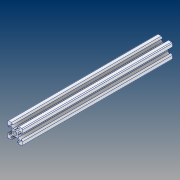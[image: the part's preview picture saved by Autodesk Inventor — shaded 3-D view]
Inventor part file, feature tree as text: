
AUTODESK INVENTOR PART (.ipt)
format: ipt  version: 2021 (Build 250183000, 183)  size: 164,352 bytes
history: native  units: mm
features: extrude x1, sketch x1
ambient origin geometry x8: Origin, YZ Plane, XZ Plane, XY Plane, X Axis, Y Axis, Z Axis, Center Point
bodies: Solid1 (feature_tree)
feature tree (2):
  extrude  "Extrusion1"  Depth=200.0mm TaperAngle=0.0deg
  sketch  "Sketch1"  dims[d1=40.0mm d2=360.0deg d3=200.0mm d4=0.0mm]
